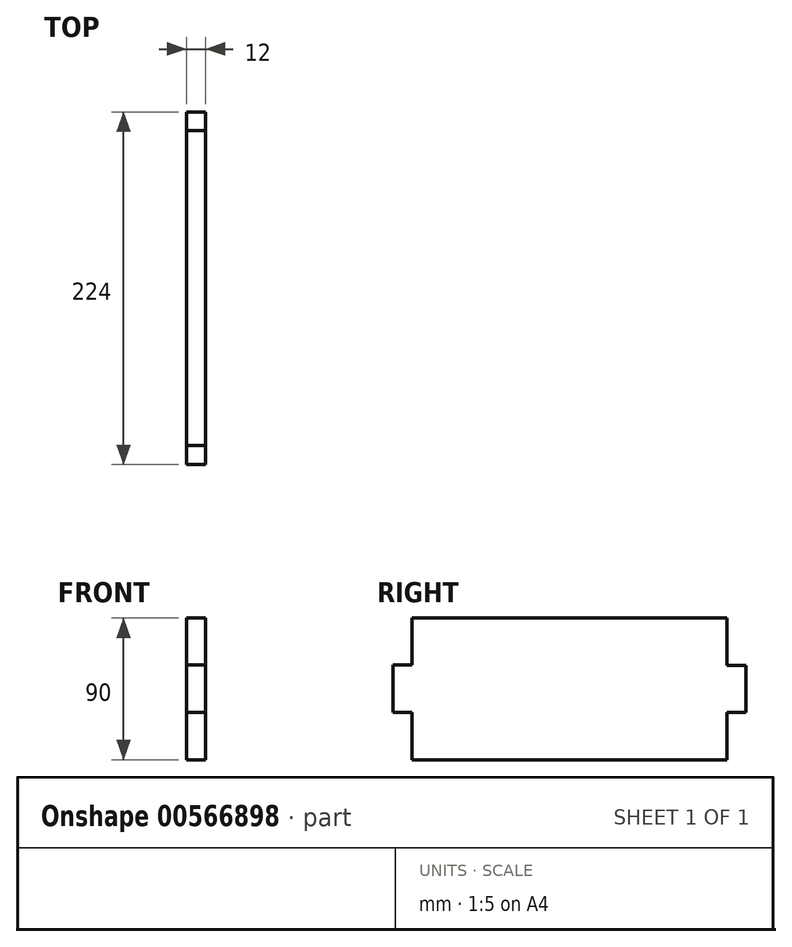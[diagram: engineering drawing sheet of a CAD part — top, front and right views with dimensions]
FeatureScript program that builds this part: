
annotation { "Feature Type Name" : "Feature", "Feature Type Description" : "" }
export const myFeature = defineFeature(function(context is Context, id is Id, definition is map)
    precondition{}
    {
        {
            var Q0;
            Q0=qCreatedBy(makeId("Right.planeOp"),FACE);
            var sketch = newSketch(context, id + "F0", { "sketchPlane" : qUnion([Q0])});
            skLineSegment(sketch, "E0", {"start": v(0, 0) * mm, "end": v(0, 30) * mm});
            skLineSegment(sketch, "E1", {"start": v(0, 30) * mm, "end": v(12, 30) * mm});
            skLineSegment(sketch, "E2", {"start": v(12, 30) * mm, "end": v(12, 60) * mm});
            skLineSegment(sketch, "E3", {"start": v(12, 60) * mm, "end": v(0, 60) * mm});
            skLineSegment(sketch, "E4", {"start": v(0, 60) * mm, "end": v(0, 90) * mm});
            skLineSegment(sketch, "E5", {"start": v(0, 90) * mm, "end": v(-200, 90) * mm});
            skLineSegment(sketch, "E6", {"start": v(0, 0) * mm, "end": v(-200, 0) * mm});
            skLineSegment(sketch, "E7", {"start": v(-200, 60.09) * mm, "end": v(-212, 60.09) * mm});
            skLineSegment(sketch, "E8", {"start": v(-212, 60.09) * mm, "end": v(-212, 30.09) * mm});
            skLineSegment(sketch, "E9", {"start": v(-200, 90) * mm, "end": v(-200, 60) * mm});
            skLineSegment(sketch, "E10", {"start": v(-212, 30.09) * mm, "end": v(-200, 30.09) * mm});
            skLineSegment(sketch, "E11", {"start": v(-200, 30.09) * mm, "end": v(-200, 0) * mm});
            skSolve(sketch);
        }
        {
            var Q0;
            Q0=makeQuery(id+"F0.imprint","IMPRINT",FACE,{"disambiguationData":[TD([[makeQuery(id+"F0.imprint","IMPRINT",EDGE,{"derivedFrom":sQuery(id+"F0.wireOp",EDGE,"E0")}),1.0]])]});
            extrude(context, id + "F1", {"entities" : qUnion([Q0]), "depth" : 12 * mm, "offsetDistance" : 25 * mm});
        }
    });
